# Revit family: NLRS_33_GM_FB_TC_STORAX_vloerluik_BV_BCB
name_source: partatom
category: Generic Models
revit_build: Autodesk Revit 2014 (Build: 20130308_1515(x64)
units: mm (PartAtom-declared; Revit-internal decimal feet)

## types (1)
- NLRS_33_GM_FB_TC_STORAX_vloerluik_BV_BCB
    Default Elevation = 1219 mm
    Manufacturer = Storax
    Model = BV
    URL = http://www.storax.nl
    belasting = 125 kN
    binnenluik = tbv betonvulling
    binnenmaat_breedte = 300 mm  [stored 0.984252 ft]
    binnenmaat_lengte = 300 mm  [stored 0.984252 ft]
    brandwerend 90 min = nee
    gasdrukveer = nee
    gewicht = 10
    geïsoleerd = nee
    materiaal = bcb_staal
    productgroep = Vloerluiken
    rubberen_afdichting = enkel
    scharnierend = nee
    sluiting = 4
    uitwendige_breedte = 435 mm  [stored 1.42717 ft]
    uitwendige_lengte = 435 mm  [stored 1.42717 ft]
    vergrendeling = nee
    vullen_met_beton = ja

note: [stored X ft] marks values corroborated as IEEE doubles in the binary element streams (Revit-internal decimal feet)

## geometry (parser evidence)
native form markers: Blend x803, Sweep x8
no freeform markers — native parametric forms only
